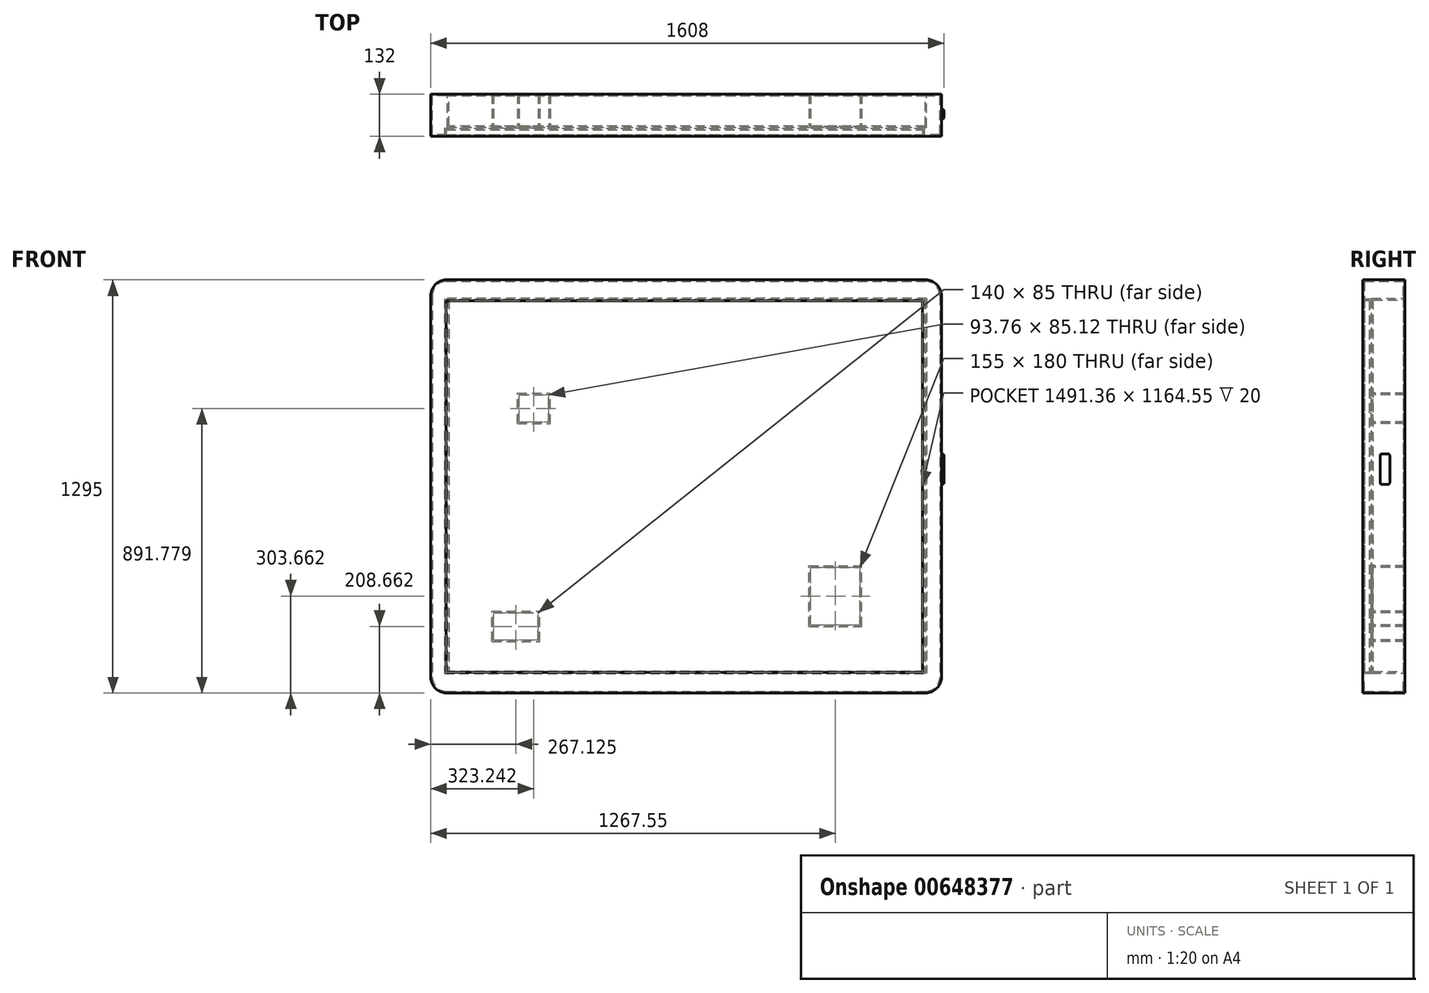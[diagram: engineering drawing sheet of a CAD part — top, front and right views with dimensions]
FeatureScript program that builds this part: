
annotation { "Feature Type Name" : "Feature", "Feature Type Description" : "" }
export const myFeature = defineFeature(function(context is Context, id is Id, definition is map)
    precondition{}
    {
        {
            var Q0;
            Q0=qCreatedBy(makeId("Front.planeOp"),FACE);
            var sketch = newSketch(context, id + "F0", { "sketchPlane" : qUnion([Q0])});
            skLineSegment(sketch, "E0.bottom", {"start": v(-794.42, 647.5) * mm, "end": v(805.58, 647.5) * mm});
            skLineSegment(sketch, "E0.top", {"start": v(-794.42, -647.5) * mm, "end": v(805.58, -647.5) * mm});
            skLineSegment(sketch, "E0.left", {"start": v(-794.42, 647.5) * mm, "end": v(-794.42, -647.5) * mm});
            skLineSegment(sketch, "E0.right", {"start": v(805.58, 647.5) * mm, "end": v(805.58, -647.5) * mm});
            skPoint(sketch, "E0.middle", {"position": v(5.58, 0) * mm});
            skSolve(sketch);
        }
        {
            var Q0;
            Q0=makeQuery(id+"F0.imprint","IMPRINT",FACE,{"disambiguationData":[TD([[makeQuery(id+"F0.imprint","IMPRINT",EDGE,{"derivedFrom":sQuery(id+"F0.wireOp",EDGE,"E0.bottom")}),-1.0]])]});
            extrude(context, id + "F1", {"entities" : qUnion([Q0]), "depth" : 132 * mm, "offsetDistance" : 25 * mm});
        }
        {
            var Q0;
            Q0=makeQuery(id+"F1.opExtrude","SWEPT_EDGE",EDGE,{"disambiguationData":[OSD([sQuery(id+"F0.wireOp",EDGE,"E0.bottom"),sQuery(id+"F0.wireOp",EDGE,"E0.left")])]});
            var Q1;
            Q1=makeQuery(id+"F1.opExtrude","SWEPT_EDGE",EDGE,{"disambiguationData":[OSD([sQuery(id+"F0.wireOp",EDGE,"E0.bottom"),sQuery(id+"F0.wireOp",EDGE,"E0.right")])]});
            var Q2;
            Q2=makeQuery(id+"F1.opExtrude","SWEPT_EDGE",EDGE,{"disambiguationData":[OSD([sQuery(id+"F0.wireOp",EDGE,"E0.top"),sQuery(id+"F0.wireOp",EDGE,"E0.right")])]});
            var Q3;
            Q3=makeQuery(id+"F1.opExtrude","SWEPT_EDGE",EDGE,{"disambiguationData":[OSD([sQuery(id+"F0.wireOp",EDGE,"E0.top"),sQuery(id+"F0.wireOp",EDGE,"E0.left")])]});
            fillet(context, id + "F2", {"entities" : qUnion([Q0, Q1, Q2, Q3]), "radius" : 50 * mm, "tangentPropagation" : true, "allowEdgeOverflow" : false});
        }
        {
            var Q0;
            Q0=makeQuery(id+"F1.opExtrude","CAP_FACE",FACE,{"disambiguationData":[OSD([sQuery(id+"F0.wireOp",EDGE,"E0.bottom"),sQuery(id+"F0.wireOp",EDGE,"E0.top"),sQuery(id+"F0.wireOp",EDGE,"E0.left"),sQuery(id+"F0.wireOp",EDGE,"E0.right")])],"isStart":false});
            cPlane(context, id + "F3", {"entities" : qUnion([Q0]), "cplaneType" : CPlaneType.OFFSET, "offset" : 0 * mm, "width" : 150 * mm, "height" : 150 * mm});
        }
        {
            var Q0;
            Q0=qCreatedBy(id+"F3.planeOp",FACE);
            var sketch = newSketch(context, id + "F4", { "sketchPlane" : qUnion([Q0])});
            skLineSegment(sketch, "E1.bottom", {"start": v(-745.68, 582.28) * mm, "end": v(745.68, 582.28) * mm});
            skLineSegment(sketch, "E1.top", {"start": v(-745.68, -582.28) * mm, "end": v(745.68, -582.28) * mm});
            skLineSegment(sketch, "E1.left", {"start": v(-745.68, 582.28) * mm, "end": v(-745.68, -582.28) * mm});
            skLineSegment(sketch, "E1.right", {"start": v(745.68, 582.28) * mm, "end": v(745.68, -582.28) * mm});
            skPoint(sketch, "E1.middle", {"position": v(0, 0) * mm});
            skSolve(sketch);
        }
        {
            var Q0;
            Q0 = qSketchRegion(id + "F4", true);
            extrude(context, id + "F5", {"entities" : qUnion([Q0]), "operationType" : NewBodyOperationType.REMOVE, "oppositeDirection" : true, "depth" : 20 * mm, "offsetDistance" : 25 * mm});
        }
        {
            var Q0;
            Q0=makeQuery(id+"F1.opExtrude","CAP_FACE",FACE,{"disambiguationData":[OSD([sQuery(id+"F0.wireOp",EDGE,"E0.bottom"),sQuery(id+"F0.wireOp",EDGE,"E0.top"),sQuery(id+"F0.wireOp",EDGE,"E0.left"),sQuery(id+"F0.wireOp",EDGE,"E0.right")])],"isStart":true});
            cPlane(context, id + "F6", {"entities" : qUnion([Q0]), "cplaneType" : CPlaneType.OFFSET, "offset" : 0 * mm, "width" : 150 * mm, "height" : 150 * mm});
        }
        {
            var Q0;
            Q0=qCreatedBy(id+"F6.planeOp",FACE);
            var sketch = newSketch(context, id + "F7", { "sketchPlane" : qUnion([Q0])});
            skLineSegment(sketch, "E2.bottom", {"start": v(-754.46, 584.48) * mm, "end": v(736.9, 584.48) * mm});
            skLineSegment(sketch, "E2.top", {"start": v(-754.46, -580.07) * mm, "end": v(736.9, -580.07) * mm});
            skLineSegment(sketch, "E2.left", {"start": v(-754.46, 584.48) * mm, "end": v(-754.46, -580.07) * mm});
            skLineSegment(sketch, "E2.right", {"start": v(736.9, 584.48) * mm, "end": v(736.9, -580.07) * mm});
            skSolve(sketch);
        }
        {
            var Q0;
            Q0 = qSketchRegion(id + "F7", true);
            extrude(context, id + "F8", {"entities" : qUnion([Q0]), "operationType" : NewBodyOperationType.REMOVE, "oppositeDirection" : true, "depth" : 100 * mm, "offsetDistance" : 25 * mm});
        }
        {
            var Q0;
            Q0=makeQuery(id+"F8.boolean.opBoolean","COPY",FACE,{"derivedFrom":makeQuery(id+"F8.opExtrude","CAP_FACE",FACE,{"disambiguationData":[OSD([sQuery(id+"F7.wireOp",EDGE,"E2.bottom"),sQuery(id+"F7.wireOp",EDGE,"E2.top"),sQuery(id+"F7.wireOp",EDGE,"E2.left"),sQuery(id+"F7.wireOp",EDGE,"E2.right")])],"isStart":false})});
            cPlane(context, id + "F9", {"entities" : qUnion([Q0]), "cplaneType" : CPlaneType.OFFSET, "offset" : 0 * mm, "width" : 150 * mm, "height" : 150 * mm});
        }
        {
            var Q0;
            Q0=qCreatedBy(id+"F9.planeOp",FACE);
            var sketch = newSketch(context, id + "F10", { "sketchPlane" : qUnion([Q0])});
            skLineSegment(sketch, "E3.bottom", {"start": v(602.3, -486.34) * mm, "end": v(452.3, -486.34) * mm});
            skLineSegment(sketch, "E3.top", {"start": v(602.3, -391.34) * mm, "end": v(452.3, -391.34) * mm});
            skLineSegment(sketch, "E3.left", {"start": v(602.3, -486.34) * mm, "end": v(602.3, -391.34) * mm});
            skLineSegment(sketch, "E3.right", {"start": v(452.3, -486.34) * mm, "end": v(452.3, -391.34) * mm});
            skPoint(sketch, "E3.middle", {"position": v(527.3, -438.84) * mm});
            skLineSegment(sketch, "E4.bottom", {"start": v(523.06, 196.72) * mm, "end": v(419.3, 196.72) * mm});
            skLineSegment(sketch, "E4.top", {"start": v(523.06, 291.84) * mm, "end": v(419.3, 291.84) * mm});
            skLineSegment(sketch, "E4.left", {"start": v(523.06, 196.72) * mm, "end": v(523.06, 291.84) * mm});
            skLineSegment(sketch, "E4.right", {"start": v(419.3, 196.72) * mm, "end": v(419.3, 291.84) * mm});
            skPoint(sketch, "E4.middle", {"position": v(471.18, 244.28) * mm});
            skLineSegment(sketch, "E5.bottom", {"start": v(-390.63, -438.84) * mm, "end": v(-555.63, -438.84) * mm});
            skLineSegment(sketch, "E5.top", {"start": v(-390.63, -248.84) * mm, "end": v(-555.63, -248.84) * mm});
            skLineSegment(sketch, "E5.left", {"start": v(-390.63, -438.84) * mm, "end": v(-390.63, -248.84) * mm});
            skLineSegment(sketch, "E5.right", {"start": v(-555.63, -438.84) * mm, "end": v(-555.63, -248.84) * mm});
            skPoint(sketch, "E5.middle", {"position": v(-473.13, -343.84) * mm});
            skSolve(sketch);
        }
        {
            var Q0;
            Q0 = qSketchRegion(id + "F10", true);
            extrude(context, id + "F11", {"entities" : qUnion([Q0]), "operationType" : NewBodyOperationType.ADD, "depth" : 100 * mm, "offsetDistance" : 25 * mm});
        }
        {
            var Q0;
            Q0=makeQuery(id+"F11.opExtrude","CAP_FACE",FACE,{"disambiguationData":[OSD([sQuery(id+"F10.wireOp",EDGE,"E3.bottom"),sQuery(id+"F10.wireOp",EDGE,"E3.top"),sQuery(id+"F10.wireOp",EDGE,"E3.left"),sQuery(id+"F10.wireOp",EDGE,"E3.right")])],"isStart":false});
            var Q1;
            Q1=makeQuery(id+"F11.opExtrude","CAP_FACE",FACE,{"disambiguationData":[OSD([sQuery(id+"F10.wireOp",EDGE,"E4.bottom"),sQuery(id+"F10.wireOp",EDGE,"E4.top"),sQuery(id+"F10.wireOp",EDGE,"E4.left"),sQuery(id+"F10.wireOp",EDGE,"E4.right")])],"isStart":false});
            var Q2;
            Q2=makeQuery(id+"F11.opExtrude","CAP_FACE",FACE,{"disambiguationData":[OSD([sQuery(id+"F10.wireOp",EDGE,"E5.bottom"),sQuery(id+"F10.wireOp",EDGE,"E5.top"),sQuery(id+"F10.wireOp",EDGE,"E5.left"),sQuery(id+"F10.wireOp",EDGE,"E5.right")])],"isStart":false});
            shell(context, id + "F12", {"entities" : qUnion([Q0, Q1, Q2]), "thickness" : 5 * mm});
        }
        {
            var Q0;
            Q0=makeQuery(id+"F1.opExtrude","SWEPT_FACE",FACE,{"disambiguationData":[OSD([sQuery(id+"F0.wireOp",EDGE,"E0.right")])]});
            var sketch = newSketch(context, id + "F13", { "sketchPlane" : qUnion([Q0])});
            skLineSegment(sketch, "E6.bottom", {"start": v(-77.89, 101.6) * mm, "end": v(-47.63, 101.6) * mm});
            skLineSegment(sketch, "E6.top", {"start": v(-77.89, 6.49) * mm, "end": v(-47.63, 6.49) * mm});
            skLineSegment(sketch, "E6.left", {"start": v(-77.89, 101.6) * mm, "end": v(-77.89, 6.49) * mm});
            skLineSegment(sketch, "E6.right", {"start": v(-47.63, 101.6) * mm, "end": v(-47.63, 6.49) * mm});
            skPoint(sketch, "E6.middle", {"position": v(-62.76, 54.04) * mm});
            skSolve(sketch);
        }
        {
            var Q0;
            Q0 = qSketchRegion(id + "F13", true);
            extrude(context, id + "F14", {"entities" : qUnion([Q0]), "operationType" : NewBodyOperationType.ADD, "depth" : 8 * mm, "offsetDistance" : 25 * mm});
        }
        {
            var Q0;
            Q0=makeQuery(id+"F14.opExtrude","SWEPT_EDGE",EDGE,{"disambiguationData":[OSD([sQuery(id+"F13.wireOp",EDGE,"E6.bottom"),sQuery(id+"F13.wireOp",EDGE,"E6.right")])]});
            var Q1;
            Q1=makeQuery(id+"F14.opExtrude","SWEPT_EDGE",EDGE,{"disambiguationData":[OSD([sQuery(id+"F13.wireOp",EDGE,"E6.bottom"),sQuery(id+"F13.wireOp",EDGE,"E6.left")])]});
            var Q2;
            Q2=makeQuery(id+"F14.opExtrude","SWEPT_EDGE",EDGE,{"disambiguationData":[OSD([sQuery(id+"F13.wireOp",EDGE,"E6.top"),sQuery(id+"F13.wireOp",EDGE,"E6.left")])]});
            var Q3;
            Q3=makeQuery(id+"F14.opExtrude","SWEPT_EDGE",EDGE,{"disambiguationData":[OSD([sQuery(id+"F13.wireOp",EDGE,"E6.top"),sQuery(id+"F13.wireOp",EDGE,"E6.right")])]});
            var Q4;
            Q4=makeQuery(id+"F14.opExtrude","CAP_EDGE",EDGE,{"disambiguationData":[OSD([sQuery(id+"F13.wireOp",EDGE,"E6.bottom")])],"isStart":false});
            var Q5;
            Q5=makeQuery(id+"F14.opExtrude","CAP_EDGE",EDGE,{"disambiguationData":[OSD([sQuery(id+"F13.wireOp",EDGE,"E6.left")])],"isStart":false});
            var Q6;
            Q6=makeQuery(id+"F14.opExtrude","CAP_EDGE",EDGE,{"disambiguationData":[OSD([sQuery(id+"F13.wireOp",EDGE,"E6.right")])],"isStart":false});
            var Q7;
            Q7=makeQuery(id+"F14.opExtrude","CAP_EDGE",EDGE,{"disambiguationData":[OSD([sQuery(id+"F13.wireOp",EDGE,"E6.top")])],"isStart":false});
            fillet(context, id + "F15", {"entities" : qUnion([Q0, Q1, Q2, Q3, Q4, Q5, Q6, Q7]), "radius" : 5 * mm, "tangentPropagation" : true, "allowEdgeOverflow" : false});
        }
        {
            var Q0;
            Q0=makeQuery(id+"F14.opExtrude","CAP_FACE",FACE,{"disambiguationData":[OSD([sQuery(id+"F13.wireOp",EDGE,"E6.bottom"),sQuery(id+"F13.wireOp",EDGE,"E6.top"),sQuery(id+"F13.wireOp",EDGE,"E6.left"),sQuery(id+"F13.wireOp",EDGE,"E6.right")])],"isStart":false});
            var sketch = newSketch(context, id + "F16", { "sketchPlane" : qUnion([Q0])});
            skLineSegment(sketch, "E7", {"start": v(-63.28, 60.6) * mm, "end": v(-63.28, 56.1) * mm});
            skArc(sketch, "E8", {"start": v(-59.87, 57.95) * mm, "mid": v(-63.46, 52.23) * mm, "end": v(-66.5, 58.27) * mm});
            skSolve(sketch);
        }
        {
            var Q0;
            Q0=sQuery(id+"F16.wireOp",EDGE,"E8");
            var Q1;
            Q1=sQuery(id+"F16.wireOp",EDGE,"E7");
            extrude(context, id + "F17", {"bodyType" : ToolBodyType.SURFACE, "surfaceEntities" : qUnion([Q0, Q1]), "depth" : .5 * mm, "offsetDistance" : 25 * mm});
        }
    });
